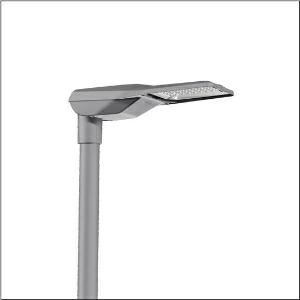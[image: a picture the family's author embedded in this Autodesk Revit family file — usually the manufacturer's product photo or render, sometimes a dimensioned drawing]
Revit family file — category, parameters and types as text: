
# Revit family: streetlight_sl_21_iq_mini___st0_5a_5xe2b41g08hb_4387
name_source: partatom
category: Lighting Fixtures
units: mm (PartAtom-declared; Revit-internal decimal feet)

## family parameters
Cut with Voids When Loaded = No
Host = Face
Light Source = No
Part Type = Normal
Room Calculation Point = No
Round Connector Dimension = Use Diameter
Shared = No

## types (1)
- --- (1 x LED, 9860 lm, 70.9 W, 4000K)
    Apparent Load = 71 VA
    CIE Flux Codes = 41 75 97 100 100
    Color Rendering = 70
    Color Temperature = 4000K
    Default Elevation = 1800 mm
    Description = Streetlight SL 21 iQ mini, mast luminaire, primary light control with lens, of PMMA, primary optical cover: cover, of toughened safety glass, transparent, light distribution: ST0.5a, light emission: direct distribution, primary light characteristic: asymmetric, installation type: post-top, side-entry, LED, High Power LED, rated luminous flux: 9.860lm, luminous efficacy: 139lm/W, light colour: 740, colour temperature: 4000K, control: Street-Remote, Auto-Match, Temp-Guard, Lumen-Switch, Night-Set, Smart-Wire, Light-Fading, Desk-Remote (wireless, voltage-free reading and setting of iQ features in the workshop via application-optimized NFC function/RFID function), optimised constant luminous flux control (CLO 2.0), presetting dimming linear, mains connection: 220..240V, AC, 50/60Hz, start of lifetime: 71W, end of service life: 75W, reduction: 31W, luminaire housing, of diecast aluminium, powder-coated, Siteco® metallic grey (DB 702S), corrosivity category C5 mid according to DIN EN ISO 12944, please order mast flange separately, inclination adjustable: 0°, 5°, 10°, 15°, sealing non-destructively replaceable, multi-level sealing system, length: 628mm, width: 235mm, height: 110mm, mast flange for spigot size: 42mm (side-entry): 5XC10008XM4, 60/48mm (side-entry/post-top): 5XC10108XM2, 76/60mm (side-entry/post-top): 5XC10108XM1, protection rating (complete): IP66, insulation class (complete): insulation class II (safety insulation), certification: CE, ENEC, ENEC+, VDE, impact resistance: IK09, permissible operating ambient temperature for outdoor applications: -40..+50°C, standard-compliant lighting for roads and squares, packaging unit: 1 piece

Light Distribution: ST0.5a
    Height = 110 mm
    Lamp = 1 x LED
    Lamp Light Flux = 9860 lm
    Lamp Power = 70.9 W
    Lamp count = 1
    Length = 625 mm
    Luminous efficacy = 139 lm/W
    Manufacturer = Siteco
    ModVariant = No
    Model = 5XE2B41G08HB
    Number of Poles = 1
    OnlyDefault = Yes
    Power Factor = 1
    Product Name = Streetlight SL 21 iQ mini | ST0.5a
    Product group = mast luminaire | pylon top
    ProductGroupID = 6100
    Protection Class = Protection class II
    Protection Degree = IP 66
    RLX_Detail_Level = 1
    RLX_Emergency_Light_Flux = 0 lm
    RLX_Emergency_Type = 0
    RLX_Emergency_Type_DB = No
    RlxData = <blob elided: 103413 chars, md5=d84f30bc>
    Socket = socket
    Standby Power = 0 W
    System Light Flux = 9860 lm
    System Power = 71 W
    Type Comments = factory setting: luminous flux: 100 % | dim-lin: 254 | 711 mA
    Type Image = l_1003519.jpg
    URL = http://relux.com
    VarID = @adj_108689
    Voltage = 0 V
    Weight = 0.00 kg
    Width = 234 mm

## geometry (parser evidence)
native form markers: Blend x4, Sweep x9
no freeform markers — native parametric forms only
